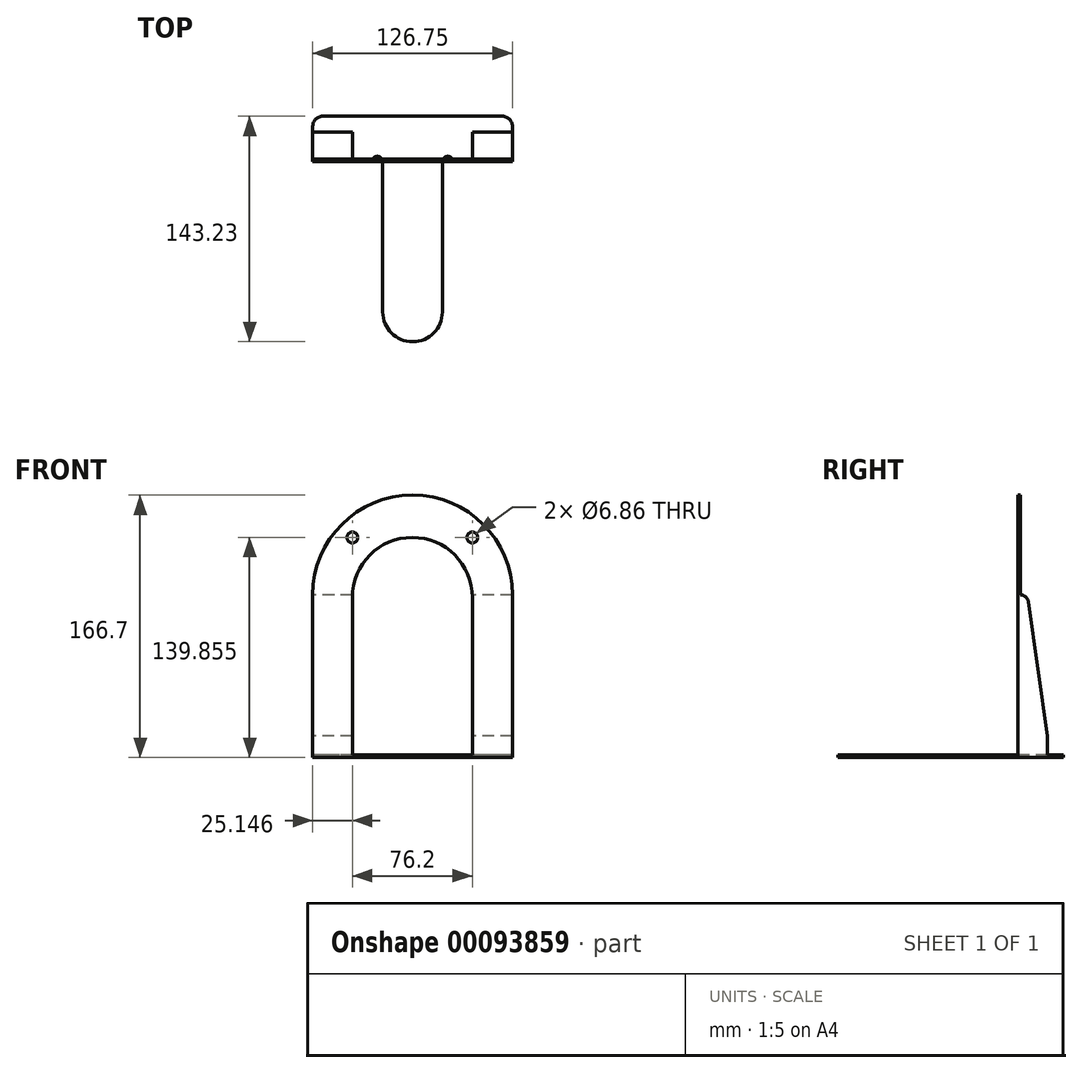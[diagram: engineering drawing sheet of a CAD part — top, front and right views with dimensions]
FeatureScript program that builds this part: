
annotation { "Feature Type Name" : "Feature", "Feature Type Description" : "" }
export const myFeature = defineFeature(function(context is Context, id is Id, definition is map)
    precondition{}
    {
        {
            var Q0;
            Q0=qCreatedBy(makeId("Right.planeOp"),FACE);
            var sketch = newSketch(context, id + "F0", { "sketchPlane" : qUnion([Q0])});
            skLineSegment(sketch, "E0", {"start": v(15.05, 65.31) * mm, "end": v(15.05, -19.6) * mm});
            skLineSegment(sketch, "E1", {"start": v(15.05, 65.31) * mm, "end": v(16.65, 65.31) * mm});
            skLineSegment(sketch, "E2", {"start": v(16.65, 65.31) * mm, "end": v(16.65, 1.97) * mm});
            skLineSegment(sketch, "E3", {"start": v(33.85, -87.75) * mm, "end": v(33.85, -99.79) * mm});
            skLineSegment(sketch, "E4", {"start": v(33.85, -99.79) * mm, "end": v(43.98, -99.79) * mm});
            skLineSegment(sketch, "E5", {"start": v(43.98, -99.79) * mm, "end": v(43.98, -101.39) * mm});
            skLineSegment(sketch, "E6", {"start": v(15.05, -99.79) * mm, "end": v(15.05, -19.6) * mm});
            skLineSegment(sketch, "E7", {"start": v(43.98, -101.39) * mm, "end": v(-99.25, -101.39) * mm});
            skLineSegment(sketch, "E8", {"start": v(-99.25, -101.39) * mm, "end": v(-99.25, -99.79) * mm});
            skLineSegment(sketch, "E9", {"start": v(-99.25, -99.79) * mm, "end": v(15.05, -99.79) * mm});
            skLineSegment(sketch, "E10", {"start": v(33.85, -87.75) * mm, "end": v(21.68, -2.4) * mm});
            skLineSegment(sketch, "E11", {"start": v(16.65, 1.97) * mm, "end": v(16.65, 1.97) * mm});
            skPoint(sketch, "E12.visualSharp", {"position": v(21.06, 1.97) * mm});
            skArc(sketch, "E12.filletArc", {"start": v(21.68, -2.4) * mm, "mid": v(19.98, 0.72) * mm, "end": v(16.65, 1.97) * mm});
            skSolve(sketch);
        }
        {
            var Q0;
            Q0=makeQuery(id+"F0.imprint","IMPRINT",FACE,{"disambiguationData":[TD([[makeQuery(id+"F0.imprint","IMPRINT",EDGE,{"derivedFrom":sQuery(id+"F0.wireOp",EDGE,"E0")}),1.0]])]});
            extrude(context, id + "F1", {"entities" : qUnion([Q0]), "depth" : 126.75 * mm});
        }
        {
            var Q0;
            Q0=makeQuery(id+"F1.opExtrude","SWEPT_FACE",FACE,{"disambiguationData":[OSD([sQuery(id+"F0.wireOp",EDGE,"E9")])]});
            var sketch = newSketch(context, id + "F2", { "sketchPlane" : qUnion([Q0])});
            skLineSegment(sketch, "E13", {"start": v(63.37, -99.25) * mm, "end": v(63.5, -99.25) * mm});
            skLineSegment(sketch, "E14", {"start": v(82.3, -80.45) * mm, "end": v(82.3, 15.05) * mm});
            skLineSegment(sketch, "E15", {"start": v(63.37, -99.25) * mm, "end": v(63.25, -99.25) * mm});
            skLineSegment(sketch, "E16", {"start": v(44.45, -80.45) * mm, "end": v(44.45, 15.05) * mm});
            skPoint(sketch, "E17.visualSharp", {"position": v(82.3, -99.25) * mm});
            skArc(sketch, "E17.filletArc", {"start": v(63.5, -99.25) * mm, "mid": v(76.8, -93.74) * mm, "end": v(82.3, -80.45) * mm});
            skPoint(sketch, "E18.visualSharp", {"position": v(44.45, -99.25) * mm});
            skArc(sketch, "E18.filletArc", {"start": v(44.45, -80.45) * mm, "mid": v(49.96, -93.74) * mm, "end": v(63.25, -99.25) * mm});
            skSolve(sketch);
        }
        {
            var Q0;
            {var subQ5=sQuery(id+"F2.wireOp",EDGE,"E16");Q0=makeQuery(id+"F2.imprint","IMPRINT",FACE,{"disambiguationData":[TD([[makeQuery(id+"F2.imprint","IMPRINT",EDGE,{"derivedFrom":subQ5}),1.0]])]});}
            var Q1;
            {var subQ4=sQuery(id+"F2.wireOp",EDGE,"E14");Q1=makeQuery(id+"F2.imprint","IMPRINT",FACE,{"disambiguationData":[TD([[makeQuery(id+"F2.imprint","IMPRINT",EDGE,{"derivedFrom":subQ4}),-1.0]])]});}
            extrude(context, id + "F3", {"entities" : qUnion([Q0, Q1]), "operationType" : NewBodyOperationType.REMOVE, "endBound" : BoundingType.THROUGH_ALL, "oppositeDirection" : true, "depth" : 25.4 * mm});
        }
        {
            var Q0;
            {var subQ0=sQuery(id+"F0.wireOp",EDGE,"E9");var subQ1=sQuery(id+"F0.wireOp",EDGE,"E6");var subQ2=makeQuery(id+"F1.opExtrude","SWEPT_EDGE",EDGE,{"disambiguationData":[OSD([subQ1,subQ0])]});Q0=makeQuery(id+"F3.boolean.opBoolean","MERGE",FACE,{"derivedFrom":[makeQuery(id+"F1.opExtrude","SWEPT_FACE",FACE,{"disambiguationData":[OSD([sQuery(id+"F0.wireOp",EDGE,"E0"),subQ1])]}),makeQuery(id+"F3.opExtrude","SWEPT_FACE",FACE,{"disambiguationData":[OSD([subQ1,subQ0]),TDD([makeQuery(id+"F2.imprint","IMPRINT",EDGE,{"disambiguationData":[TD([[makeQuery(id+"F2.imprint","INTERSECT",VERTEX,{"derivedFrom":[subQ2,makeQuery(id+"F1.opExtrude","CAP_EDGE",EDGE,{"disambiguationData":[OSD([subQ0])],"isStart":true})]}),1.0]])],"derivedFrom":subQ2})])]}),makeQuery(id+"F3.opExtrude","SWEPT_FACE",FACE,{"disambiguationData":[OSD([subQ1,subQ0]),TDD([makeQuery(id+"F2.imprint","IMPRINT",EDGE,{"disambiguationData":[TD([[makeQuery(id+"F2.imprint","INTERSECT",VERTEX,{"derivedFrom":[subQ2,makeQuery(id+"F1.opExtrude","CAP_EDGE",EDGE,{"disambiguationData":[OSD([subQ0])],"isStart":false})]}),-1.0]])],"derivedFrom":subQ2})])]})]});}
            var sketch = newSketch(context, id + "F4", { "sketchPlane" : qUnion([Q0])});
            skLineSegment(sketch, "E19", {"start": v(25.15, -101.39) * mm, "end": v(25.15, 2.9) * mm});
            skLineSegment(sketch, "E20", {"start": v(101.35, 2.9) * mm, "end": v(101.35, -101.39) * mm});
            skPoint(sketch, "E21.endSnap0", {"position": v(63.37, 65.31) * mm});
            skLineSegment(sketch, "E22", {"start": v(63.25, 38.47) * mm, "end": v(63.37, 38.47) * mm});
            skLineSegment(sketch, "E23", {"start": v(101.35, 2.9) * mm, "end": v(101.35, 0.37) * mm});
            skLineSegment(sketch, "E24", {"start": v(63.37, 38.47) * mm, "end": v(63.25, 38.47) * mm});
            skLineSegment(sketch, "E25", {"start": v(25.15, 2.9) * mm, "end": v(25.15, 0.37) * mm});
            skPoint(sketch, "E26.visualSharp", {"position": v(25.15, 38.47) * mm});
            skArc(sketch, "E26.filletArc", {"start": v(63.25, 38.47) * mm, "mid": v(36.3, 27.3) * mm, "end": v(25.15, 0.37) * mm});
            skPoint(sketch, "E27.visualSharp", {"position": v(101.35, 38.47) * mm});
            skArc(sketch, "E27.filletArc", {"start": v(101.35, 0.37) * mm, "mid": v(90.19, 27.3) * mm, "end": v(63.25, 38.47) * mm});
            skLineSegment(sketch, "E28", {"start": v(0, 0) * mm, "end": v(0, -12.4) * mm});
            skLineSegment(sketch, "E29", {"start": v(126.75, 0.37) * mm, "end": v(126.75, -12.4) * mm});
            skLineSegment(sketch, "E30", {"start": v(63.5, 65.31) * mm, "end": v(63.37, 65.31) * mm});
            skLineSegment(sketch, "E31", {"start": v(63.25, 65.31) * mm, "end": v(63.37, 65.31) * mm});
            skPoint(sketch, "E32.visualSharp", {"position": v(126.75, 65.31) * mm});
            skArc(sketch, "E32.filletArc", {"start": v(126.75, 2.07) * mm, "mid": v(108.22, 46.79) * mm, "end": v(63.5, 65.31) * mm});
            skPoint(sketch, "E33.visualSharp", {"position": v(0, 65.31) * mm});
            skArc(sketch, "E33.filletArc", {"start": v(63.25, 65.31) * mm, "mid": v(18.52, 46.79) * mm, "end": v(0, 2.07) * mm});
            skCircle(sketch, "E34", {"center": v(25.15, 38.47) * mm, "radius": 3.43 * mm});
            skCircle(sketch, "E35", {"center": v(101.35, 38.47) * mm, "radius": 3.43 * mm});
            skLineSegment(sketch, "E36", {"start": v(44.45, -99.79) * mm, "end": v(25.15, -99.79) * mm});
            skLineSegment(sketch, "E37", {"start": v(25.15, -99.79) * mm, "end": v(101.35, -99.79) * mm});
            skSolve(sketch);
        }
        {
            var Q0;
            {var subQ0=sQuery(id+"F4.wireOp",EDGE,"E33.filletArc");Q0=makeQuery(id+"F4.imprint","IMPRINT",FACE,{"disambiguationData":[TD([[makeQuery(id+"F4.imprint","IMPRINT",EDGE,{"derivedFrom":subQ0}),-1.0]])]});}
            var Q1;
            {var subQ0=sQuery(id+"F4.wireOp",EDGE,"E32.filletArc");Q1=makeQuery(id+"F4.imprint","IMPRINT",FACE,{"disambiguationData":[TD([[makeQuery(id+"F4.imprint","IMPRINT",EDGE,{"derivedFrom":subQ0}),-1.0]])]});}
            var Q2;
            {var subQ0=sQuery(id+"F4.wireOp",EDGE,"E26.filletArc");Q2=makeQuery(id+"F4.imprint","IMPRINT",FACE,{"disambiguationData":[TD([[makeQuery(id+"F4.imprint","IMPRINT",EDGE,{"derivedFrom":subQ0}),1.0]])]});}
            var Q3;
            Q3=makeQuery(id+"F4.imprint","IMPRINT",FACE,{"disambiguationData":[TD([[makeQuery(id+"F4.imprint","IMPRINT",EDGE,{"derivedFrom":sQuery(id+"F4.wireOp",EDGE,"E34")}),1.0]])]});
            var Q4;
            Q4=makeQuery(id+"F4.imprint","IMPRINT",FACE,{"disambiguationData":[TD([[makeQuery(id+"F4.imprint","IMPRINT",EDGE,{"derivedFrom":sQuery(id+"F4.wireOp",EDGE,"E35")}),1.0]])]});
            extrude(context, id + "F5", {"entities" : qUnion([Q0, Q1, Q2, Q3, Q4]), "operationType" : NewBodyOperationType.REMOVE, "endBound" : BoundingType.THROUGH_ALL, "oppositeDirection" : true, "depth" : 25.4 * mm});
        }
        {
            var Q0;
            Q0=makeQuery(id+"F1.opExtrude","SWEPT_FACE",FACE,{"disambiguationData":[OSD([sQuery(id+"F0.wireOp",EDGE,"E7")])]});
            var sketch = newSketch(context, id + "F6", { "sketchPlane" : qUnion([Q0])});
            skLineSegment(sketch, "E38", {"start": v(44.45, -15.05) * mm, "end": v(44.45, -15.05) * mm});
            skLineSegment(sketch, "E39", {"start": v(41.02, -18.48) * mm, "end": v(41.02, -18.48) * mm});
            skLineSegment(sketch, "E40", {"start": v(37.6, -15.05) * mm, "end": v(37.6, -15.05) * mm});
            skPoint(sketch, "E41.visualSharp", {"position": v(44.45, -18.48) * mm});
            skArc(sketch, "E41.filletArc", {"start": v(41.02, -18.48) * mm, "mid": v(43.45, -17.48) * mm, "end": v(44.45, -15.05) * mm});
            skPoint(sketch, "E42.visualSharp", {"position": v(37.6, -18.48) * mm});
            skArc(sketch, "E42.filletArc", {"start": v(37.6, -15.05) * mm, "mid": v(38.6, -17.48) * mm, "end": v(41.02, -18.48) * mm});
            skLineSegment(sketch, "E43", {"start": v(126.75, -15.05) * mm, "end": v(126.75, -37.63) * mm});
            skLineSegment(sketch, "E44", {"start": v(120.4, -43.98) * mm, "end": v(90.2, -43.98) * mm});
            skPoint(sketch, "E45.visualSharp", {"position": v(126.75, -43.98) * mm});
            skArc(sketch, "E45.filletArc", {"start": v(120.4, -43.98) * mm, "mid": v(124.89, -42.12) * mm, "end": v(126.75, -37.63) * mm});
            skLineSegment(sketch, "E46", {"start": v(82.3, -15.05) * mm, "end": v(82.3, -15.05) * mm});
            skLineSegment(sketch, "E47", {"start": v(85.73, -18.48) * mm, "end": v(85.73, -18.48) * mm});
            skLineSegment(sketch, "E48", {"start": v(89.15, -15.05) * mm, "end": v(89.15, -15.05) * mm});
            skPoint(sketch, "E49.visualSharp", {"position": v(82.3, -18.48) * mm});
            skArc(sketch, "E49.filletArc", {"start": v(82.3, -15.05) * mm, "mid": v(83.3, -17.48) * mm, "end": v(85.73, -18.48) * mm});
            skPoint(sketch, "E50.visualSharp", {"position": v(89.15, -18.48) * mm});
            skArc(sketch, "E50.filletArc", {"start": v(85.73, -18.48) * mm, "mid": v(88.15, -17.48) * mm, "end": v(89.15, -15.05) * mm});
            skLineSegment(sketch, "E51", {"start": v(0, -15.05) * mm, "end": v(0, -37.63) * mm});
            skLineSegment(sketch, "E52", {"start": v(6.35, -43.98) * mm, "end": v(27.88, -43.98) * mm});
            skPoint(sketch, "E53.visualSharp", {"position": v(0, -43.98) * mm});
            skArc(sketch, "E53.filletArc", {"start": v(0, -37.63) * mm, "mid": v(1.86, -42.12) * mm, "end": v(6.35, -43.98) * mm});
            skSolve(sketch);
        }
        {
            var Q0;
            {var subQ0=sQuery(id+"F6.wireOp",EDGE,"E53.filletArc");Q0=makeQuery(id+"F6.imprint","IMPRINT",FACE,{"disambiguationData":[TD([[makeQuery(id+"F6.imprint","IMPRINT",EDGE,{"derivedFrom":subQ0}),-1.0]])]});}
            var Q1;
            {var subQ0=sQuery(id+"F6.wireOp",EDGE,"E41.filletArc");Q1=makeQuery(id+"F6.imprint","IMPRINT",FACE,{"disambiguationData":[TD([[makeQuery(id+"F6.imprint","IMPRINT",EDGE,{"derivedFrom":subQ0}),1.0]])]});}
            var Q2;
            {var subQ0=sQuery(id+"F6.wireOp",EDGE,"E49.filletArc");Q2=makeQuery(id+"F6.imprint","IMPRINT",FACE,{"disambiguationData":[TD([[makeQuery(id+"F6.imprint","IMPRINT",EDGE,{"derivedFrom":subQ0}),1.0]])]});}
            var Q3;
            {var subQ0=sQuery(id+"F6.wireOp",EDGE,"E45.filletArc");Q3=makeQuery(id+"F6.imprint","IMPRINT",FACE,{"disambiguationData":[TD([[makeQuery(id+"F6.imprint","IMPRINT",EDGE,{"derivedFrom":subQ0}),-1.0]])]});}
            extrude(context, id + "F7", {"entities" : qUnion([Q0, Q1, Q2, Q3]), "operationType" : NewBodyOperationType.REMOVE, "oppositeDirection" : true, "depth" : 25.4 * mm});
        }
    });
